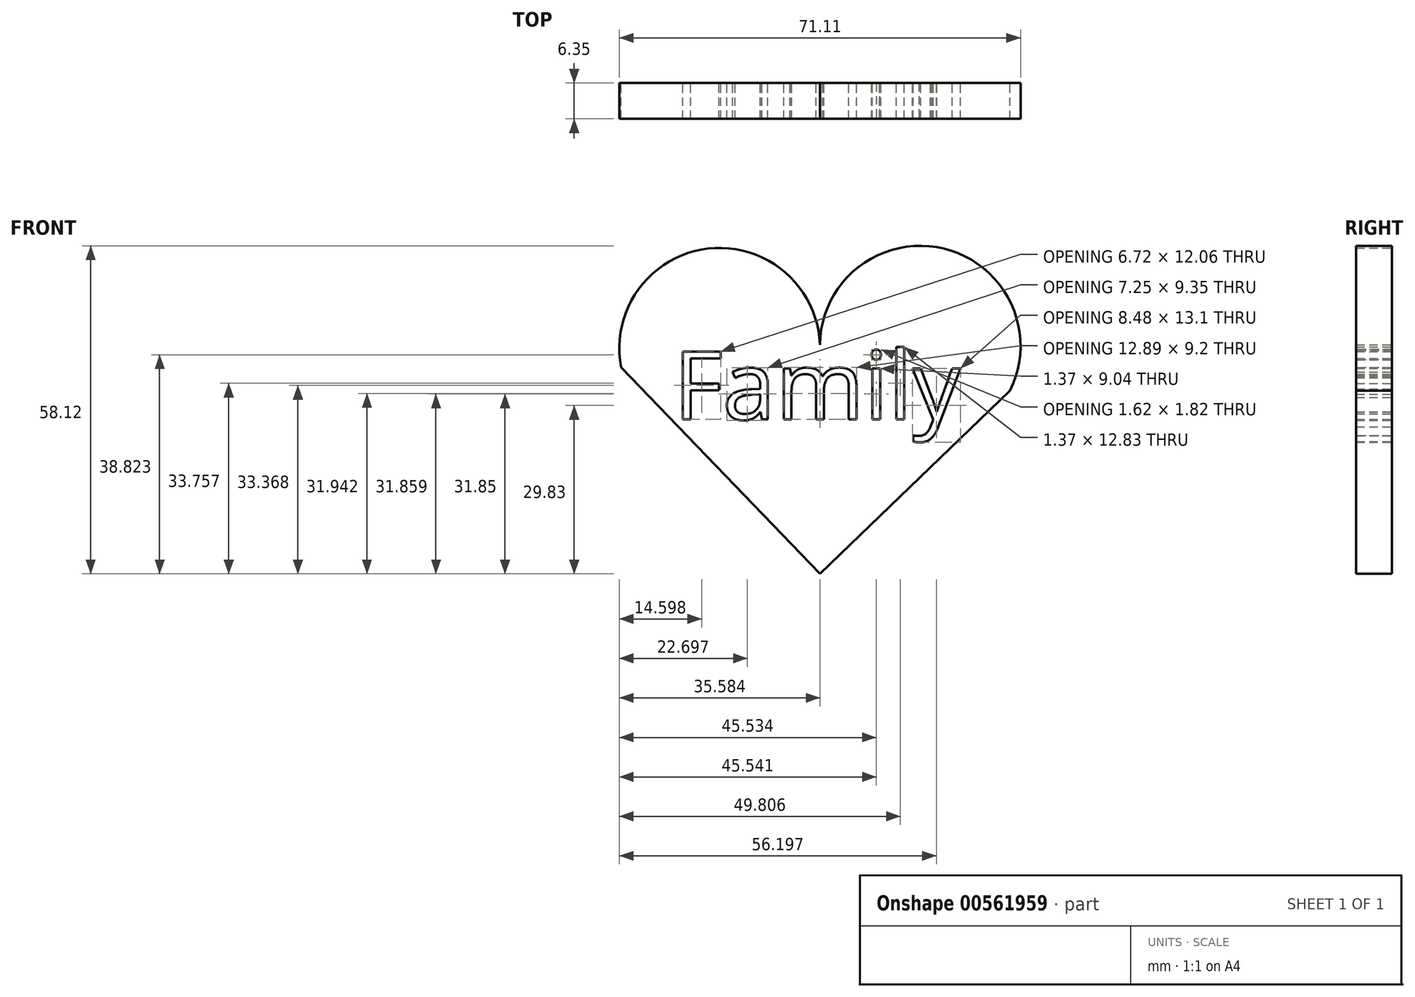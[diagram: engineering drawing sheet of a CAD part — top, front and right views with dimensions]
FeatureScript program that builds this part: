
annotation { "Feature Type Name" : "Feature", "Feature Type Description" : "" }
export const myFeature = defineFeature(function(context is Context, id is Id, definition is map)
    precondition{}
    {
        {
            var Q0;
            Q0=qCreatedBy(makeId("Front.planeOp"),FACE);
            var sketch = newSketch(context, id + "F0", { "sketchPlane" : qUnion([Q0])});
            skLineSegment(sketch, "E0", {"start": v(0, 0) * mm, "end": v(-35.23, 36.6) * mm});
            skLineSegment(sketch, "E1", {"start": v(0, 0) * mm, "end": v(33.7, 32.44) * mm});
            skArc(sketch, "E2", {"start": v(0, 40.58) * mm, "mid": v(-19.76, 57.63) * mm, "end": v(-35.23, 36.6) * mm});
            skArc(sketch, "E3", {"start": v(33.7, 32.44) * mm, "mid": v(21.95, 57.63) * mm, "end": v(0, 40.58) * mm});
            skSolve(sketch);
        }
        {
            var Q0;
            Q0=makeQuery(id+"F0.imprint","IMPRINT",FACE,{"disambiguationData":[TD([[makeQuery(id+"F0.imprint","IMPRINT",EDGE,{"derivedFrom":sQuery(id+"F0.wireOp",EDGE,"E0")}),-1.0]])]});
            extrude(context, id + "F1", {"entities" : qUnion([Q0]), "depth" : 6.35 * mm, "offsetDistance" : 25.4 * mm});
        }
        {
            var Q0;
            Q0=qCreatedBy(makeId("Front.planeOp"),FACE);
            var sketch = newSketch(context, id + "F2", { "sketchPlane" : qUnion([Q0])});
            skText(sketch, "E4", { "text": "Family", "fontName": "OpenSans-Regular.ttf"});
            const initialGuessF2  = {"E4": [-0.02597, 0.02734, 1, 0, 0.01216]};
            skSetInitialGuess(sketch, initialGuessF2);
            skSolve(sketch);
        }
        {
            var Q0;
            Q0 = qSketchRegion(id + "F2", true);
            extrude(context, id + "F3", {"entities" : qUnion([Q0]), "operationType" : NewBodyOperationType.REMOVE, "depth" : 25.4 * mm, "offsetDistance" : 25.4 * mm});
        }
    });
